# Revit family: Gira_2280600
name_source: partatom
category: Electrical Fixtures
revit_build: Autodesk Revit 2017 (Build: 20160225_1515(x64)
units: mm (PartAtom-declared; Revit-internal decimal feet)

## family parameters
Cut with Voids When Loaded = No
Host = Face
Maintain Annotation Orientation = Yes
Part Type = Normal
Room Calculation Point = No
Round Connector Dimension = Use Diameter
Shared = No

## types (1)
- RDS FM radio speaker System 55 stainl.steel
    Assembly arrangement = Basic element with housing top
    Available = No
    BIM (1) = https://media.stage.bim.site
    Category = Electronic insert for domestic switching devices
    Colour = Stainless steel
    Data sheet (1) = https://katalog.gira.de
    Default Elevation = 1219 mm
    Description = RDS FM radio spk. Sys55 SST,RDS flush-mounted radio with a speaker,Operating top unit in black glass appearance,Stainless steel,Features:,- FM radio with RDS display for flush-mounted installation.,- The RDS flush-mounted radio consists of a radio insert with operating top unit and speaker insert with cover.,- The radio insert is compactly mounted in a flush-mounted insert and can therefore be installed in a single device box.,- The speaker can be installed in combination with the radio insert or offset in a device box. Two loudspeakers can be connected to the radio insert.,- The radio automatically detects connected speakers and switches between stereo and mono mode.,- With a corresponding RDS signal, the display of the operating top unit shows the station name, the transmission frequency and the time.,- Operation of the radio is using the capacitive buttons of the operating top unit. Operation only requires a light touching of the symbols.,- The RDS flush-mounted radio has two station presets, upon each of which a station setting can simply be saved and called up with the button actuation.,- For example, the radio can be switched on via the auxiliary input with a light switch or automatic control switch together with the room lighting.,- External audio sources, for example an MP3 player, can be connected to the radio via the stereo AUX input of the radio. For connection to the external audio source, an additional phono insert is required which is connected to the AUX terminals of the radio insert.,- The docking station insert is connected directly to the stereo AUX input for music playback.,- In sleep mode the radio switches off automatically 30 minutes after switching on.,,Notes :,- Reception interference can result in combination with additional electronic devices under one cover plate.
    GTIN = 4010337021070
    HAN = 2280600
    Halogen free = No
    HeinzeBIM = https://bimportal.heinze.de
    Manufacturer = Gira
    Manufacturer URL = https://www.gira.de
    Material = Other
    Material quality = Other
    Model = Radio
    Mounting method = Flush mounted (plaster)
    Name = RDS FM radio speaker System 55 stainl.steel
    Surface finishing = Glossy
    Surface protection = Other
    Type of fastening = Mounting with claw and screw
    URL = http://katalog.gira.de

## geometry (parser evidence)
native form markers: Sweep x3
no freeform markers — native parametric forms only
